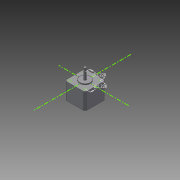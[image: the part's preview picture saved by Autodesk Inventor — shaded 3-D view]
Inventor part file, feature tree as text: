
AUTODESK INVENTOR PART (.ipt)
format: ipt  version: 2015 (Build 190159000, 159)  size: 106,496 bytes
history: native  units: in
note: dims shown in document units (in); Inventor stores cm internally (conversion verified against a paired STEP export)
features: sketch x4, extrude x3
ambient origin geometry x8: Origin, YZ Plane, XZ Plane, XY Plane, X Axis, Y Axis, Z Axis, Center Point
bodies: Solid1 (feature_tree)
feature tree (7):
  extrude  "Extrusion1"  Depth=1.6654in
  extrude  "Extrusion2"  Depth=0.125in
  extrude  "Extrusion3"  Depth=0.125in
  sketch  "Sketch4"  dims[d6=0.125in d7=0.125in d8=0.125in d9=0.125in d10=1.3386in d11=0.0in d12=0.8661in d13=0.0787in d14=0.0in d15=0.1969in d16=0.8661in d17=0.0in d18=1.2205in d19=1.2205in]
  sketch  "Sketch1"  dims[d0=1.6654in d1=1.6654in]
  sketch  "Sketch2"  dims[d2=0.125in d3=0.125in]
  sketch  "Sketch3"  dims[d4=0.125in d5=0.125in]
